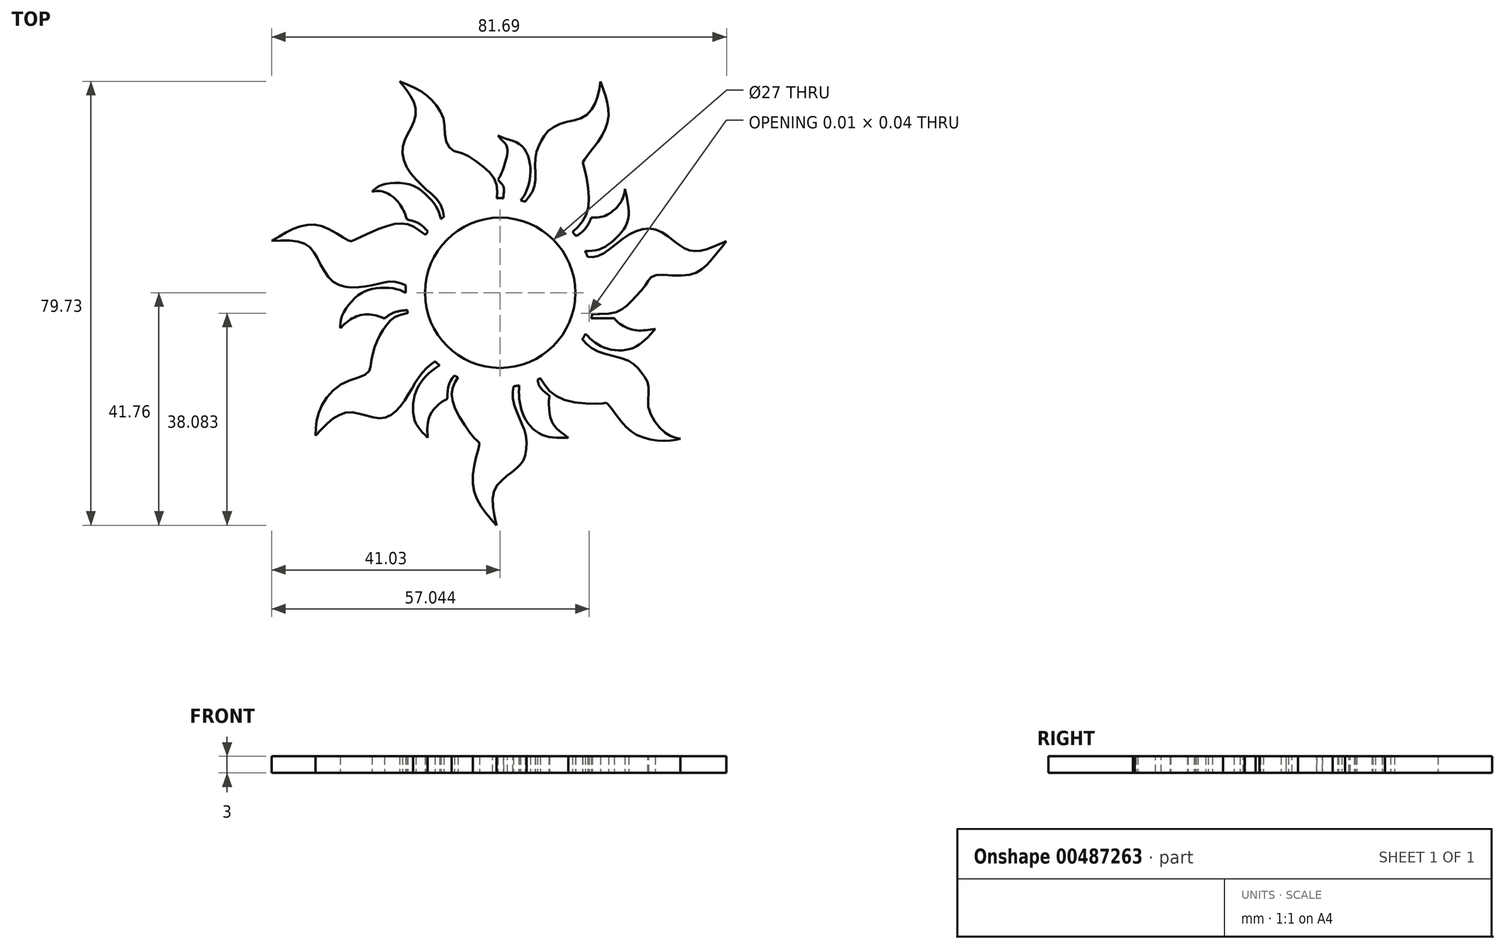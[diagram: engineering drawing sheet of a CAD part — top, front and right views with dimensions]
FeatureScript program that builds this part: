
annotation { "Feature Type Name" : "Feature", "Feature Type Description" : "" }
export const myFeature = defineFeature(function(context is Context, id is Id, definition is map)
    precondition{}
    {
        {
            var Q0;
            Q0=qCreatedBy(makeId("Top.planeOp"),FACE);
            var sketch = newSketch(context, id + "F0", { "sketchPlane" : qUnion([Q0])});
            skCircle(sketch, "E0", {"center": v(0, 0) * mm, "radius": 16.43 * mm});
            skFitSpline(sketch, "E1", {"points": [v(15.09, 6.52) * mm, v(17.93, 6.75) * mm, v(23.31, 10.54) * mm, v(28.2, 11.27) * mm, v(32.53, 8.33) * mm, v(35.77, 7.53) * mm, v(40.66, 9.3) * mm], "startDerivative": vector(20.7, -2.43) * mm, "endDerivative": vector(29.04, 13.5) * mm});
            skFitSpline(sketch, "E2", {"points": [v(40.66, 9.3) * mm, v(37.32, 5.25) * mm, v(33.66, 3.16) * mm, v(27.6, 3.06) * mm, v(26.2, 1.5) * mm, v(23.25, -1.79) * mm, v(20.23, -3.64) * mm, v(16.01, -3.7) * mm, v(16.02, -3.66) * mm], "startDerivative": vector(-21.04, -27.36) * mm, "endDerivative": vector(2.3, 2.87) * mm});
            skFitSpline(sketch, "E3", {"points": [v(14.9, -6.91) * mm, v(18.38, -9.74) * mm, v(23.79, -9.93) * mm, v(27.83, -6.5) * mm], "startDerivative": vector(9.64, -10.51) * mm, "endDerivative": vector(10.5, 12.28) * mm});
            skLineSegment(sketch, "E4", {"start": v(15.87, -4.26) * mm, "end": v(16.33, -4.55) * mm});
            skLineSegment(sketch, "E5", {"start": v(16.33, -4.55) * mm, "end": v(20.49, -4.55) * mm});
            skFitSpline(sketch, "E6", {"points": [v(20.49, -4.55) * mm, v(20.83, -5) * mm, v(23.5, -6.57) * mm, v(27.83, -6.5) * mm], "startDerivative": vector(1.38, -2.4) * mm, "endDerivative": vector(9.81, 1.54) * mm});
            skCircle(sketch, "E7", {"center": v(0, 0) * mm, "radius": 13.5 * mm});
            skFitSpline(sketch, "E8", {"points": [v(6.97, -14.88) * mm, v(11.19, -19.1) * mm, v(18.82, -19.82) * mm, v(19.17, -19.82) * mm, v(21.65, -22.98) * mm, v(25.17, -25.81) * mm, v(29.83, -26.58) * mm, v(32.34, -26.25) * mm], "startDerivative": vector(16.54, -28.35) * mm, "endDerivative": vector(19.42, 3.94) * mm});
            skFitSpline(sketch, "E9", {"points": [v(14.37, -7.96) * mm, v(17.42, -10.5) * mm, v(22.97, -12.18) * mm, v(25.4, -14.36) * mm, v(26.67, -16.8) * mm, v(26.67, -20.75) * mm, v(29.86, -25.3) * mm, v(32.34, -26.25) * mm], "startDerivative": vector(17.67, -20.06) * mm, "endDerivative": vector(20.16, -4.15) * mm});
            skFitSpline(sketch, "E10", {"points": [v(2.51, -16.24) * mm, v(2.3, -18.97) * mm, v(3.6, -22.87) * mm, v(4.64, -25.72) * mm, v(4.5, -29.22) * mm, v(3.47, -31.03) * mm, v(1.14, -32.98) * mm, v(-1.13, -35.77) * mm, v(-0.67, -41.76) * mm], "startDerivative": vector(-4.55, -23.18) * mm, "endDerivative": vector(8.62, -40.16) * mm});
            skFitSpline(sketch, "E11", {"points": [v(-7.28, -14.73) * mm, v(-8.56, -19.37) * mm, v(-4.04, -26.68) * mm, v(-3.72, -27.04) * mm, v(-4.91, -34.2) * mm, v(-0.67, -41.76) * mm], "startDerivative": vector(-13.63, -20.7) * mm, "endDerivative": vector(23.69, -25.95) * mm});
            skFitSpline(sketch, "E12", {"points": [v(-11.25, -11.97) * mm, v(-14.16, -14.56) * mm, v(-17.38, -19.63) * mm, v(-21.4, -22.53) * mm, v(-27.36, -21.48) * mm, v(-33.16, -25.67) * mm], "startDerivative": vector(-18.11, -13.16) * mm, "endDerivative": vector(-24.28, -26.37) * mm});
            skFitSpline(sketch, "E13", {"points": [v(-33.16, -25.67) * mm, v(-32.52, -21.32) * mm, v(-28.5, -16.41) * mm, v(-23.82, -14.4) * mm, v(-23.18, -12.47) * mm, v(-22.37, -9.24) * mm, v(-20.92, -6.5) * mm, v(-19.15, -4.5) * mm, v(-16.05, -3.53) * mm], "startDerivative": vector(0.9, 31) * mm, "endDerivative": vector(28.99, 5.54) * mm});
            skFitSpline(sketch, "E14", {"points": [v(-16.4, 1.1) * mm, v(-19.15, 2.02) * mm, v(-22.37, 1.5) * mm, v(-26.12, 0.98) * mm, v(-29.88, 1.89) * mm, v(-32.6, 5.78) * mm, v(-34.93, 8.76) * mm, v(-41.03, 9.34) * mm], "startDerivative": vector(-22.22, 10.49) * mm, "endDerivative": vector(-39.66, -1.53) * mm});
            skFitSpline(sketch, "E15", {"points": [v(-41.03, 9.34) * mm, v(-35.94, 11.92) * mm, v(-31.49, 11.75) * mm, v(-27.16, 9.34) * mm, v(-26.53, 9.34) * mm, v(-20.92, 11.8) * mm, v(-16.6, 12.3) * mm, v(-13, 10.06) * mm], "startDerivative": vector(30.55, 18.52) * mm, "endDerivative": vector(24.38, -19.45) * mm});
            skFitSpline(sketch, "E16", {"points": [v(12.57, 10.58) * mm, v(15.8, 15.26) * mm, v(14.96, 22.9) * mm, v(14.96, 23.69) * mm, v(18.2, 28.1) * mm, v(19.44, 32.76) * mm, v(18.04, 37.97) * mm], "startDerivative": vector(23.1, 20.05) * mm, "endDerivative": vector(-10.65, 29.55) * mm});
            skFitSpline(sketch, "E17", {"points": [v(18.04, 37.97) * mm, v(17.14, 34.17) * mm, v(14.94, 31.57) * mm, v(11.54, 30.57) * mm, v(8.54, 28.97) * mm, v(7.14, 26.77) * mm, v(6.34, 24.37) * mm, v(6.34, 20.57) * mm, v(5.8, 18.2) * mm, v(4.07, 15.92) * mm], "startDerivative": vector(-4.73, -31.85) * mm, "endDerivative": vector(-18.77, -21.37) * mm});
            skFitSpline(sketch, "E18", {"points": [v(-0.67, 16.42) * mm, v(-0.67, 19.64) * mm, v(-3.1, 22.72) * mm, v(-6.95, 25.12) * mm, v(-7.95, 25.33) * mm, v(-9.57, 26.8) * mm, v(-10.09, 30.87) * mm, v(-11.76, 34.05) * mm, v(-14.18, 36.2) * mm, v(-18.04, 37.97) * mm], "startDerivative": vector(4.06, 29.94) * mm, "endDerivative": vector(-32.4, 12.8) * mm});
            skFitSpline(sketch, "E19", {"points": [v(-18.04, 37.97) * mm, v(-16.66, 36.2) * mm, v(-15.23, 33.35) * mm, v(-15.7, 30.22) * mm, v(-17.1, 27.5) * mm, v(-17.42, 24.22) * mm, v(-15.54, 20.82) * mm, v(-13.03, 18.37) * mm, v(-10.74, 15.92) * mm, v(-10.07, 12.99) * mm], "startDerivative": vector(14.23, -17.63) * mm, "endDerivative": vector(2.73, -28.56) * mm});
            skFitSpline(sketch, "E20", {"points": [v(3.47, -16.06) * mm, v(3.47, -19.38) * mm, v(4.92, -23.3) * mm, v(7.97, -25.67) * mm, v(12.23, -26.01) * mm], "startDerivative": vector(-1.03, -13.94) * mm, "endDerivative": vector(17.02, 0.51) * mm});
            skFitSpline(sketch, "E21", {"points": [v(12.23, -26.01) * mm, v(10.54, -24.73) * mm, v(9.12, -22.7) * mm, v(8.81, -18.9) * mm, v(8.81, -18.5) * mm, v(7.36, -17.21) * mm, v(6.6, -15.05) * mm], "startDerivative": vector(-10.14, 7.27) * mm, "endDerivative": vector(-2.08, 13.04) * mm});
            skFitSpline(sketch, "E22", {"points": [v(-10.42, -12.7) * mm, v(-13.25, -14.88) * mm, v(-15.3, -18.28) * mm, v(-15.32, -22.98) * mm, v(-13.03, -26.01) * mm], "startDerivative": vector(-12.59, -8.37) * mm, "endDerivative": vector(11.31, -11.02) * mm});
            skFitSpline(sketch, "E23", {"points": [v(-13.03, -26.01) * mm, v(-13.03, -23.76) * mm, v(-11.94, -20.95) * mm, v(-9.76, -19.2) * mm, v(-9.54, -19.04) * mm, v(-9.3, -16.8) * mm, v(-7.86, -14.43) * mm], "startDerivative": vector(-0.75, 12.54) * mm, "endDerivative": vector(9.27, 10.95) * mm});
            skFitSpline(sketch, "E24", {"points": [v(-16.43, -0.31) * mm, v(-18.37, 0.6) * mm, v(-22.3, 0.83) * mm, v(-25.66, -0.58) * mm, v(-28.36, -4.09) * mm, v(-28.73, -6.37) * mm], "startDerivative": vector(-10.49, 6.37) * mm, "endDerivative": vector(-0.29, -12.72) * mm});
            skFitSpline(sketch, "E25", {"points": [v(-28.73, -6.37) * mm, v(-26.87, -4.8) * mm, v(-23.9, -3.87) * mm, v(-20.79, -4.61) * mm], "startDerivative": vector(5.5, 5.5) * mm, "endDerivative": vector(8.8, -3.25) * mm});
            skFitSpline(sketch, "E26", {"points": [v(-20.79, -4.61) * mm, v(-18.99, -3.52) * mm, v(-16.14, -3.07) * mm], "startDerivative": vector(3.59, 2.74) * mm, "endDerivative": vector(5.66, 0.41) * mm});
            skFitSpline(sketch, "E27", {"points": [v(-10.44, 12.69) * mm, v(-11.43, 15.37) * mm, v(-13.65, 17.96) * mm, v(-16.7, 19.58) * mm, v(-21.58, 19.25) * mm, v(-22.98, 18.18) * mm], "startDerivative": vector(-3.97, 14.4) * mm, "endDerivative": vector(-7.06, -7.97) * mm});
            skFitSpline(sketch, "E28", {"points": [v(-22.98, 18.18) * mm, v(-21.03, 18.18) * mm, v(-18.85, 16.86) * mm, v(-17.36, 14.8) * mm, v(-16.75, 13.17) * mm], "startDerivative": vector(8.19, 1.03) * mm, "endDerivative": vector(2.24, -7.1) * mm});
            skFitSpline(sketch, "E29", {"points": [v(-16.75, 13.17) * mm, v(-14.53, 12.42) * mm, v(-12.61, 10.53) * mm], "startDerivative": vector(4.81, -1.04) * mm, "endDerivative": vector(3.47, -4.2) * mm});
            skFitSpline(sketch, "E30", {"points": [v(14.64, 7.46) * mm, v(17.95, 7.86) * mm, v(21, 10.03) * mm, v(23, 13.17) * mm, v(22.42, 18.7) * mm], "startDerivative": vector(14.97, 0.09) * mm, "endDerivative": vector(-4.65, 20.38) * mm});
            skFitSpline(sketch, "E31", {"points": [v(13.1, 9.92) * mm, v(15.09, 11.27) * mm, v(16.4, 13.51) * mm], "startDerivative": vector(4.45, 2.36) * mm, "endDerivative": vector(2.19, 4.83) * mm});
            skFitSpline(sketch, "E32", {"points": [v(16.4, 13.51) * mm, v(19.02, 13.92) * mm, v(21.74, 16.4) * mm, v(22.42, 18.7) * mm], "startDerivative": vector(8.08, 0.03) * mm, "endDerivative": vector(1.1, 7.43) * mm});
            skFitSpline(sketch, "E33", {"points": [v(3.32, 16.1) * mm, v(4.71, 18.27) * mm, v(5.42, 22.63) * mm, v(3.67, 26.56) * mm, v(-0.39, 28.24) * mm], "startDerivative": vector(7.4, 9.52) * mm, "endDerivative": vector(-16.34, 8.3) * mm});
            skFitSpline(sketch, "E34", {"points": [v(0.45, 16.43) * mm, v(0.57, 19.14) * mm, v(-0.39, 20.39) * mm], "startDerivative": vector(0.79, 5.48) * mm, "endDerivative": vector(-2.5, 4.38) * mm});
            skFitSpline(sketch, "E35", {"points": [v(-0.39, 20.39) * mm, v(0.73, 22.88) * mm, v(1.22, 26.23) * mm, v(-0.39, 28.24) * mm], "startDerivative": vector(4.41, 4.72) * mm, "endDerivative": vector(-5.76, 7.62) * mm});
            skCircle(sketch, "E36", {"center": v(0, 0) * mm, "radius": 16.99 * mm});
            skSolve(sketch);
        }
        {
            var Q0;
            {var subQ0=sQuery(id+"F0.wireOp",EDGE,"E33");var subQ1=sQuery(id+"F0.wireOp",EDGE,"E0");var subQ2=makeQuery(id+"F0.imprint","INTERSECT",VERTEX,{"derivedFrom":[subQ1,subQ0]});Q0=makeQuery(id+"F0.imprint","IMPRINT",FACE,{"disambiguationData":[TD([[makeQuery(id+"F0.imprint","IMPRINT",EDGE,{"disambiguationData":[TD([[subQ2,-1.0]])],"derivedFrom":subQ1}),-1.0]])]});}
            var Q1;
            {var subQ0=sQuery(id+"F0.wireOp",EDGE,"E16");var subQ1=sQuery(id+"F0.wireOp",EDGE,"E0");var subQ2=makeQuery(id+"F0.imprint","INTERSECT",VERTEX,{"derivedFrom":[subQ1,subQ0]});Q1=makeQuery(id+"F0.imprint","IMPRINT",FACE,{"disambiguationData":[TD([[makeQuery(id+"F0.imprint","IMPRINT",EDGE,{"disambiguationData":[TD([[subQ2,-1.0]])],"derivedFrom":subQ1}),-1.0]])]});}
            var Q2;
            {var subQ0=sQuery(id+"F0.wireOp",EDGE,"E17");var subQ1=sQuery(id+"F0.wireOp",EDGE,"E16");var subQ2=makeQuery(id+"F0.imprint","INTERSECT",VERTEX,{"derivedFrom":[subQ1,subQ0]});Q2=makeQuery(id+"F0.imprint","IMPRINT",FACE,{"disambiguationData":[TD([[makeQuery(id+"F0.imprint","IMPRINT",EDGE,{"disambiguationData":[TD([[subQ2,1.0]])],"derivedFrom":subQ1}),1.0]])]});}
            var Q3;
            {var subQ0=sQuery(id+"F0.wireOp",EDGE,"E32");Q3=makeQuery(id+"F0.imprint","IMPRINT",FACE,{"disambiguationData":[TD([[makeQuery(id+"F0.imprint","IMPRINT",EDGE,{"derivedFrom":subQ0}),-1.0]])]});}
            var Q4;
            {var subQ0=sQuery(id+"F0.wireOp",EDGE,"E30");var subQ1=sQuery(id+"F0.wireOp",EDGE,"E0");var subQ2=makeQuery(id+"F0.imprint","INTERSECT",VERTEX,{"derivedFrom":[subQ1,subQ0]});Q4=makeQuery(id+"F0.imprint","IMPRINT",FACE,{"disambiguationData":[TD([[makeQuery(id+"F0.imprint","IMPRINT",EDGE,{"disambiguationData":[TD([[subQ2,-1.0]])],"derivedFrom":subQ1}),-1.0]])]});}
            var Q5;
            {var subQ0=sQuery(id+"F0.wireOp",EDGE,"E28");Q5=makeQuery(id+"F0.imprint","IMPRINT",FACE,{"disambiguationData":[TD([[makeQuery(id+"F0.imprint","IMPRINT",EDGE,{"derivedFrom":subQ0}),1.0]])]});}
            var Q6;
            {var subQ0=sQuery(id+"F0.wireOp",EDGE,"E15");var subQ1=sQuery(id+"F0.wireOp",EDGE,"E14");var subQ2=makeQuery(id+"F0.imprint","INTERSECT",VERTEX,{"derivedFrom":[subQ1,subQ0]});Q6=makeQuery(id+"F0.imprint","IMPRINT",FACE,{"disambiguationData":[TD([[makeQuery(id+"F0.imprint","IMPRINT",EDGE,{"disambiguationData":[TD([[subQ2,1.0]])],"derivedFrom":subQ1}),-1.0]])]});}
            var Q7;
            {var subQ0=sQuery(id+"F0.wireOp",EDGE,"E25");Q7=makeQuery(id+"F0.imprint","IMPRINT",FACE,{"disambiguationData":[TD([[makeQuery(id+"F0.imprint","IMPRINT",EDGE,{"derivedFrom":subQ0}),1.0]])]});}
            var Q8;
            {var subQ0=sQuery(id+"F0.wireOp",EDGE,"E13");var subQ1=sQuery(id+"F0.wireOp",EDGE,"E12");var subQ2=makeQuery(id+"F0.imprint","INTERSECT",VERTEX,{"derivedFrom":[subQ1,subQ0]});Q8=makeQuery(id+"F0.imprint","IMPRINT",FACE,{"disambiguationData":[TD([[makeQuery(id+"F0.imprint","IMPRINT",EDGE,{"disambiguationData":[TD([[subQ2,1.0]])],"derivedFrom":subQ1}),-1.0]])]});}
            var Q9;
            {var subQ0=sQuery(id+"F0.wireOp",EDGE,"E27");var subQ1=sQuery(id+"F0.wireOp",EDGE,"E0");var subQ2=makeQuery(id+"F0.imprint","INTERSECT",VERTEX,{"derivedFrom":[subQ1,subQ0]});Q9=makeQuery(id+"F0.imprint","IMPRINT",FACE,{"disambiguationData":[TD([[makeQuery(id+"F0.imprint","IMPRINT",EDGE,{"disambiguationData":[TD([[subQ2,-1.0]])],"derivedFrom":subQ1}),-1.0]])]});}
            var Q10;
            {var subQ0=sQuery(id+"F0.wireOp",EDGE,"E18");var subQ1=sQuery(id+"F0.wireOp",EDGE,"E0");var subQ2=makeQuery(id+"F0.imprint","INTERSECT",VERTEX,{"derivedFrom":[subQ1,subQ0]});Q10=makeQuery(id+"F0.imprint","IMPRINT",FACE,{"disambiguationData":[TD([[makeQuery(id+"F0.imprint","IMPRINT",EDGE,{"disambiguationData":[TD([[subQ2,-1.0]])],"derivedFrom":subQ1}),-1.0]])]});}
            var Q11;
            {var subQ0=sQuery(id+"F0.wireOp",EDGE,"E14");var subQ1=sQuery(id+"F0.wireOp",EDGE,"E0");var subQ2=makeQuery(id+"F0.imprint","INTERSECT",VERTEX,{"derivedFrom":[subQ1,subQ0]});Q11=makeQuery(id+"F0.imprint","IMPRINT",FACE,{"disambiguationData":[TD([[makeQuery(id+"F0.imprint","IMPRINT",EDGE,{"disambiguationData":[TD([[subQ2,1.0]])],"derivedFrom":subQ1}),-1.0]])]});}
            var Q12;
            {var subQ0=sQuery(id+"F0.wireOp",EDGE,"E24");var subQ1=sQuery(id+"F0.wireOp",EDGE,"E0");var subQ2=makeQuery(id+"F0.imprint","INTERSECT",VERTEX,{"derivedFrom":[subQ1,subQ0]});Q12=makeQuery(id+"F0.imprint","IMPRINT",FACE,{"disambiguationData":[TD([[makeQuery(id+"F0.imprint","IMPRINT",EDGE,{"disambiguationData":[TD([[subQ2,-1.0]])],"derivedFrom":subQ1}),-1.0]])]});}
            var Q13;
            {var subQ0=sQuery(id+"F0.wireOp",EDGE,"E12");var subQ1=sQuery(id+"F0.wireOp",EDGE,"E0");var subQ2=makeQuery(id+"F0.imprint","INTERSECT",VERTEX,{"derivedFrom":[subQ1,subQ0]});Q13=makeQuery(id+"F0.imprint","IMPRINT",FACE,{"disambiguationData":[TD([[makeQuery(id+"F0.imprint","IMPRINT",EDGE,{"disambiguationData":[TD([[subQ2,1.0]])],"derivedFrom":subQ1}),-1.0]])]});}
            var Q14;
            {var subQ0=sQuery(id+"F0.wireOp",EDGE,"E19");var subQ1=sQuery(id+"F0.wireOp",EDGE,"E18");var subQ2=makeQuery(id+"F0.imprint","INTERSECT",VERTEX,{"derivedFrom":[subQ1,subQ0]});Q14=makeQuery(id+"F0.imprint","IMPRINT",FACE,{"disambiguationData":[TD([[makeQuery(id+"F0.imprint","IMPRINT",EDGE,{"disambiguationData":[TD([[subQ2,1.0]])],"derivedFrom":subQ1}),1.0]])]});}
            var Q15;
            {var subQ0=sQuery(id+"F0.wireOp",EDGE,"E22");var subQ1=sQuery(id+"F0.wireOp",EDGE,"E0");var subQ2=makeQuery(id+"F0.imprint","INTERSECT",VERTEX,{"derivedFrom":[subQ1,subQ0]});Q15=makeQuery(id+"F0.imprint","IMPRINT",FACE,{"disambiguationData":[TD([[makeQuery(id+"F0.imprint","IMPRINT",EDGE,{"disambiguationData":[TD([[subQ2,-1.0]])],"derivedFrom":subQ1}),-1.0]])]});}
            var Q16;
            {var subQ0=sQuery(id+"F0.wireOp",EDGE,"E10");var subQ1=sQuery(id+"F0.wireOp",EDGE,"E0");var subQ2=makeQuery(id+"F0.imprint","INTERSECT",VERTEX,{"derivedFrom":[subQ1,subQ0]});Q16=makeQuery(id+"F0.imprint","IMPRINT",FACE,{"disambiguationData":[TD([[makeQuery(id+"F0.imprint","IMPRINT",EDGE,{"disambiguationData":[TD([[subQ2,1.0]])],"derivedFrom":subQ1}),-1.0]])]});}
            var Q17;
            {var subQ0=sQuery(id+"F0.wireOp",EDGE,"E23");var subQ1=sQuery(id+"F0.wireOp",EDGE,"E22");var subQ2=makeQuery(id+"F0.imprint","INTERSECT",VERTEX,{"derivedFrom":[subQ1,subQ0]});Q17=makeQuery(id+"F0.imprint","IMPRINT",FACE,{"disambiguationData":[TD([[makeQuery(id+"F0.imprint","IMPRINT",EDGE,{"disambiguationData":[TD([[subQ2,1.0]])],"derivedFrom":subQ1}),1.0]])]});}
            var Q18;
            {var subQ0=sQuery(id+"F0.wireOp",EDGE,"E11");var subQ1=sQuery(id+"F0.wireOp",EDGE,"E10");var subQ2=makeQuery(id+"F0.imprint","INTERSECT",VERTEX,{"derivedFrom":[subQ1,subQ0]});Q18=makeQuery(id+"F0.imprint","IMPRINT",FACE,{"disambiguationData":[TD([[makeQuery(id+"F0.imprint","IMPRINT",EDGE,{"disambiguationData":[TD([[subQ2,1.0]])],"derivedFrom":subQ1}),-1.0]])]});}
            var Q19;
            {var subQ0=sQuery(id+"F0.wireOp",EDGE,"E21");var subQ1=sQuery(id+"F0.wireOp",EDGE,"E20");var subQ2=makeQuery(id+"F0.imprint","INTERSECT",VERTEX,{"derivedFrom":[subQ1,subQ0]});Q19=makeQuery(id+"F0.imprint","IMPRINT",FACE,{"disambiguationData":[TD([[makeQuery(id+"F0.imprint","IMPRINT",EDGE,{"disambiguationData":[TD([[subQ2,1.0]])],"derivedFrom":subQ1}),1.0]])]});}
            var Q20;
            {var subQ0=sQuery(id+"F0.wireOp",EDGE,"E9");var subQ1=sQuery(id+"F0.wireOp",EDGE,"E8");var subQ2=makeQuery(id+"F0.imprint","INTERSECT",VERTEX,{"derivedFrom":[subQ1,subQ0]});Q20=makeQuery(id+"F0.imprint","IMPRINT",FACE,{"disambiguationData":[TD([[makeQuery(id+"F0.imprint","IMPRINT",EDGE,{"disambiguationData":[TD([[subQ2,1.0]])],"derivedFrom":subQ1}),1.0]])]});}
            var Q21;
            {var subQ0=sQuery(id+"F0.wireOp",EDGE,"E6");Q21=makeQuery(id+"F0.imprint","IMPRINT",FACE,{"disambiguationData":[TD([[makeQuery(id+"F0.imprint","IMPRINT",EDGE,{"derivedFrom":subQ0}),-1.0]])]});}
            var Q22;
            {var subQ0=sQuery(id+"F0.wireOp",EDGE,"E2");var subQ1=sQuery(id+"F0.wireOp",EDGE,"E1");var subQ2=makeQuery(id+"F0.imprint","INTERSECT",VERTEX,{"derivedFrom":[subQ1,subQ0]});Q22=makeQuery(id+"F0.imprint","IMPRINT",FACE,{"disambiguationData":[TD([[makeQuery(id+"F0.imprint","IMPRINT",EDGE,{"disambiguationData":[TD([[subQ2,1.0]])],"derivedFrom":subQ1}),-1.0]])]});}
            var Q23;
            {var subQ1=sQuery(id+"F0.wireOp",EDGE,"E0");var subQ5=sQuery(id+"F0.wireOp",EDGE,"E2");var subQ6=makeQuery(id+"F0.imprint","INTERSECT",VERTEX,{"disambiguationData":[OD(0.0)],"derivedFrom":[subQ1,subQ5]});Q23=makeQuery(id+"F0.imprint","IMPRINT",FACE,{"disambiguationData":[TD([[makeQuery(id+"F0.imprint","IMPRINT",EDGE,{"disambiguationData":[TD([[subQ6,1.0]])],"derivedFrom":subQ1}),-1.0]])]});}
            var Q24;
            {var subQ0=sQuery(id+"F0.wireOp",EDGE,"E20");var subQ1=sQuery(id+"F0.wireOp",EDGE,"E0");var subQ2=makeQuery(id+"F0.imprint","INTERSECT",VERTEX,{"derivedFrom":[subQ1,subQ0]});Q24=makeQuery(id+"F0.imprint","IMPRINT",FACE,{"disambiguationData":[TD([[makeQuery(id+"F0.imprint","IMPRINT",EDGE,{"disambiguationData":[TD([[subQ2,-1.0]])],"derivedFrom":subQ1}),-1.0]])]});}
            var Q25;
            {var subQ0=sQuery(id+"F0.wireOp",EDGE,"E8");var subQ1=sQuery(id+"F0.wireOp",EDGE,"E0");var subQ2=makeQuery(id+"F0.imprint","INTERSECT",VERTEX,{"derivedFrom":[subQ1,subQ0]});Q25=makeQuery(id+"F0.imprint","IMPRINT",FACE,{"disambiguationData":[TD([[makeQuery(id+"F0.imprint","IMPRINT",EDGE,{"disambiguationData":[TD([[subQ2,-1.0]])],"derivedFrom":subQ1}),-1.0]])]});}
            var Q26;
            {var subQ1=sQuery(id+"F0.wireOp",EDGE,"E4");Q26=makeQuery(id+"F0.imprint","IMPRINT",FACE,{"disambiguationData":[TD([[makeQuery(id+"F0.imprint","IMPRINT",EDGE,{"derivedFrom":subQ1}),-1.0]])]});}
            var Q27;
            {var subQ0=sQuery(id+"F0.wireOp",EDGE,"E35");Q27=makeQuery(id+"F0.imprint","IMPRINT",FACE,{"disambiguationData":[TD([[makeQuery(id+"F0.imprint","IMPRINT",EDGE,{"derivedFrom":subQ0}),-1.0]])]});}
            var Q28;
            {var subQ0=sQuery(id+"F0.wireOp",EDGE,"E1");var subQ1=sQuery(id+"F0.wireOp",EDGE,"E0");var subQ2=makeQuery(id+"F0.imprint","INTERSECT",VERTEX,{"derivedFrom":[subQ1,subQ0]});Q28=makeQuery(id+"F0.imprint","IMPRINT",FACE,{"disambiguationData":[TD([[makeQuery(id+"F0.imprint","IMPRINT",EDGE,{"disambiguationData":[TD([[subQ2,-1.0]])],"derivedFrom":subQ1}),-1.0]])]});}
            var Q29;
            {var subQ0=sQuery(id+"F0.wireOp",EDGE,"E17");var subQ1=sQuery(id+"F0.wireOp",EDGE,"E0");var subQ2=makeQuery(id+"F0.imprint","INTERSECT",VERTEX,{"derivedFrom":[subQ1,subQ0]});Q29=makeQuery(id+"F0.imprint","IMPRINT",FACE,{"disambiguationData":[TD([[makeQuery(id+"F0.imprint","IMPRINT",EDGE,{"disambiguationData":[TD([[subQ2,-1.0]])],"derivedFrom":subQ1}),-1.0]])]});}
            var Q30;
            {var subQ0=sQuery(id+"F0.wireOp",EDGE,"E16");var subQ1=sQuery(id+"F0.wireOp",EDGE,"E0");var subQ2=makeQuery(id+"F0.imprint","INTERSECT",VERTEX,{"derivedFrom":[subQ1,subQ0]});Q30=makeQuery(id+"F0.imprint","IMPRINT",FACE,{"disambiguationData":[TD([[makeQuery(id+"F0.imprint","IMPRINT",EDGE,{"disambiguationData":[TD([[subQ2,1.0]])],"derivedFrom":subQ1}),-1.0]])]});}
            var Q31;
            {var subQ0=sQuery(id+"F0.wireOp",EDGE,"E18");var subQ1=sQuery(id+"F0.wireOp",EDGE,"E0");var subQ2=makeQuery(id+"F0.imprint","INTERSECT",VERTEX,{"derivedFrom":[subQ1,subQ0]});Q31=makeQuery(id+"F0.imprint","IMPRINT",FACE,{"disambiguationData":[TD([[makeQuery(id+"F0.imprint","IMPRINT",EDGE,{"disambiguationData":[TD([[subQ2,1.0]])],"derivedFrom":subQ1}),-1.0]])]});}
            var Q32;
            {var subQ0=sQuery(id+"F0.wireOp",EDGE,"E19");var subQ1=sQuery(id+"F0.wireOp",EDGE,"E0");var subQ2=makeQuery(id+"F0.imprint","INTERSECT",VERTEX,{"derivedFrom":[subQ1,subQ0]});Q32=makeQuery(id+"F0.imprint","IMPRINT",FACE,{"disambiguationData":[TD([[makeQuery(id+"F0.imprint","IMPRINT",EDGE,{"disambiguationData":[TD([[subQ2,-1.0]])],"derivedFrom":subQ1}),-1.0]])]});}
            var Q33;
            {var subQ0=sQuery(id+"F0.wireOp",EDGE,"E15");var subQ1=sQuery(id+"F0.wireOp",EDGE,"E0");var subQ2=makeQuery(id+"F0.imprint","INTERSECT",VERTEX,{"derivedFrom":[subQ1,subQ0]});Q33=makeQuery(id+"F0.imprint","IMPRINT",FACE,{"disambiguationData":[TD([[makeQuery(id+"F0.imprint","IMPRINT",EDGE,{"disambiguationData":[TD([[subQ2,1.0]])],"derivedFrom":subQ1}),-1.0]])]});}
            var Q34;
            {var subQ0=sQuery(id+"F0.wireOp",EDGE,"E14");var subQ1=sQuery(id+"F0.wireOp",EDGE,"E0");var subQ2=makeQuery(id+"F0.imprint","INTERSECT",VERTEX,{"derivedFrom":[subQ1,subQ0]});Q34=makeQuery(id+"F0.imprint","IMPRINT",FACE,{"disambiguationData":[TD([[makeQuery(id+"F0.imprint","IMPRINT",EDGE,{"disambiguationData":[TD([[subQ2,-1.0]])],"derivedFrom":subQ1}),-1.0]])]});}
            var Q35;
            {var subQ0=sQuery(id+"F0.wireOp",EDGE,"E12");var subQ1=sQuery(id+"F0.wireOp",EDGE,"E0");var subQ2=makeQuery(id+"F0.imprint","INTERSECT",VERTEX,{"derivedFrom":[subQ1,subQ0]});Q35=makeQuery(id+"F0.imprint","IMPRINT",FACE,{"disambiguationData":[TD([[makeQuery(id+"F0.imprint","IMPRINT",EDGE,{"disambiguationData":[TD([[subQ2,-1.0]])],"derivedFrom":subQ1}),-1.0]])]});}
            var Q36;
            {var subQ0=sQuery(id+"F0.wireOp",EDGE,"E11");var subQ1=sQuery(id+"F0.wireOp",EDGE,"E0");var subQ2=makeQuery(id+"F0.imprint","INTERSECT",VERTEX,{"derivedFrom":[subQ1,subQ0]});Q36=makeQuery(id+"F0.imprint","IMPRINT",FACE,{"disambiguationData":[TD([[makeQuery(id+"F0.imprint","IMPRINT",EDGE,{"disambiguationData":[TD([[subQ2,1.0]])],"derivedFrom":subQ1}),-1.0]])]});}
            var Q37;
            {var subQ0=sQuery(id+"F0.wireOp",EDGE,"E10");var subQ1=sQuery(id+"F0.wireOp",EDGE,"E0");var subQ2=makeQuery(id+"F0.imprint","INTERSECT",VERTEX,{"derivedFrom":[subQ1,subQ0]});Q37=makeQuery(id+"F0.imprint","IMPRINT",FACE,{"disambiguationData":[TD([[makeQuery(id+"F0.imprint","IMPRINT",EDGE,{"disambiguationData":[TD([[subQ2,-1.0]])],"derivedFrom":subQ1}),-1.0]])]});}
            var Q38;
            {var subQ0=sQuery(id+"F0.wireOp",EDGE,"E8");var subQ1=sQuery(id+"F0.wireOp",EDGE,"E0");var subQ2=makeQuery(id+"F0.imprint","INTERSECT",VERTEX,{"derivedFrom":[subQ1,subQ0]});Q38=makeQuery(id+"F0.imprint","IMPRINT",FACE,{"disambiguationData":[TD([[makeQuery(id+"F0.imprint","IMPRINT",EDGE,{"disambiguationData":[TD([[subQ2,1.0]])],"derivedFrom":subQ1}),-1.0]])]});}
            var Q39;
            {var subQ0=sQuery(id+"F0.wireOp",EDGE,"E13");var subQ1=sQuery(id+"F0.wireOp",EDGE,"E0");var subQ2=makeQuery(id+"F0.imprint","INTERSECT",VERTEX,{"derivedFrom":[subQ1,subQ0]});Q39=makeQuery(id+"F0.imprint","IMPRINT",FACE,{"disambiguationData":[TD([[makeQuery(id+"F0.imprint","IMPRINT",EDGE,{"disambiguationData":[TD([[subQ2,1.0]])],"derivedFrom":subQ1}),-1.0]])]});}
            var Q40;
            {var subQ0=sQuery(id+"F0.wireOp",EDGE,"E3");var subQ1=sQuery(id+"F0.wireOp",EDGE,"E0");var subQ2=makeQuery(id+"F0.imprint","INTERSECT",VERTEX,{"derivedFrom":[subQ1,subQ0]});Q40=makeQuery(id+"F0.imprint","IMPRINT",FACE,{"disambiguationData":[TD([[makeQuery(id+"F0.imprint","IMPRINT",EDGE,{"disambiguationData":[TD([[subQ2,1.0]])],"derivedFrom":subQ1}),-1.0]])]});}
            var Q41;
            {var subQ1=sQuery(id+"F0.wireOp",EDGE,"E4");Q41=makeQuery(id+"F0.imprint","IMPRINT",FACE,{"disambiguationData":[TD([[makeQuery(id+"F0.imprint","IMPRINT",EDGE,{"derivedFrom":subQ1}),1.0]])]});}
            var Q42;
            Q42=makeQuery(id+"F0.imprint","IMPRINT",FACE,{"disambiguationData":[TD([[makeQuery(id+"F0.imprint","IMPRINT",EDGE,{"derivedFrom":sQuery(id+"F0.wireOp",EDGE,"E7")}),-1.0]])]});
            extrude(context, id + "F1", {"entities" : qUnion([Q0, Q1, Q2, Q3, Q4, Q5, Q6, Q7, Q8, Q9, Q10, Q11, Q12, Q13, Q14, Q15, Q16, Q17, Q18, Q19, Q20, Q21, Q22, Q23, Q24, Q25, Q26, Q27, Q28, Q29, Q30, Q31, Q32, Q33, Q34, Q35, Q36, Q37, Q38, Q39, Q40, Q41, Q42]), "depth" : 3 * mm});
        }
    });
